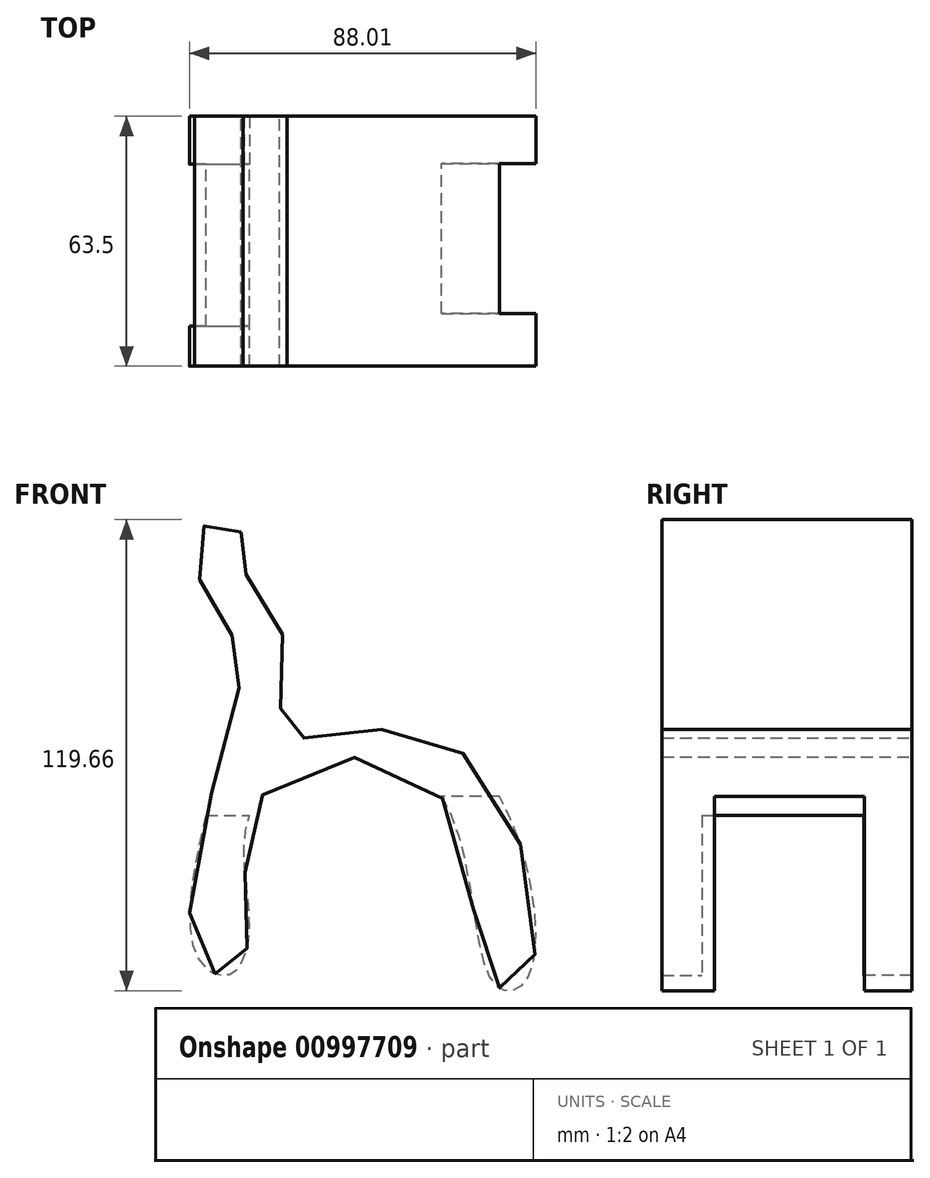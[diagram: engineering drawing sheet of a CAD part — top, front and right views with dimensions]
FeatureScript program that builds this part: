
annotation { "Feature Type Name" : "Feature", "Feature Type Description" : "" }
export const myFeature = defineFeature(function(context is Context, id is Id, definition is map)
    precondition{}
    {
        {
            var Q0;
            Q0=qCreatedBy(makeId("Front.planeOp"),FACE);
            var sketch = newSketch(context, id + "F0", { "sketchPlane" : qUnion([Q0])});
            skFitSpline(sketch, "E0", {"points": [v(-44.5, 57.5) * mm, v(-51.95, 60.33) * mm, v(-56.21, 49.33) * mm, v(-46.63, 30.89) * mm, v(-45.57, 15.64) * mm, v(-56.92, -47.15) * mm, v(-47.7, -54.95) * mm, v(-42.38, -42.18) * mm, v(-39.9, -10.26) * mm, v(3.02, -5.65) * mm, v(19.34, -56.72) * mm, v(28.2, -56.01) * mm, v(17.21, -3.87) * mm, v(-16.48, 6.77) * mm, v(-34.22, 6.77) * mm, v(-33.16, 28.4) * mm, v(-44.15, 48.98) * mm, v(-44.5, 57.5) * mm]});
            skSolve(sketch);
        }
        {
            var Q0;
            Q0=makeQuery(id+"F0.imprint","IMPRINT",FACE,{"disambiguationData":[TD([[makeQuery(id+"F0.imprint","IMPRINT",EDGE,{"derivedFrom":sQuery(id+"F0.wireOp",EDGE,"E0")}),1.0]])]});
            extrude(context, id + "F1", {"entities" : qUnion([Q0]), "depth" : 63.5 * mm, "offsetDistance" : 25.4 * mm});
        }
        {
            var Q0;
            Q0=qCreatedBy(makeId("Right.planeOp"),FACE);
            var sketch = newSketch(context, id + "F2", { "sketchPlane" : qUnion([Q0])});
            skLineSegment(sketch, "E1.bottom", {"start": v(-50.12, -9.67) * mm, "end": v(-12.03, -9.67) * mm});
            skLineSegment(sketch, "E1.top", {"start": v(-50.12, -61.45) * mm, "end": v(-12.03, -61.45) * mm});
            skLineSegment(sketch, "E1.left", {"start": v(-50.12, -9.67) * mm, "end": v(-50.12, -61.45) * mm});
            skLineSegment(sketch, "E1.right", {"start": v(-12.03, -9.67) * mm, "end": v(-12.03, -61.45) * mm});
            skSolve(sketch);
        }
        {
            var Q0;
            Q0=makeQuery(id+"F2.imprint","IMPRINT",FACE,{"disambiguationData":[TD([[makeQuery(id+"F2.imprint","IMPRINT",EDGE,{"derivedFrom":sQuery(id+"F2.wireOp",EDGE,"E1.bottom")}),-1.0]])]});
            extrude(context, id + "F3", {"entities" : qUnion([Q0]), "operationType" : NewBodyOperationType.REMOVE, "depth" : 45.97 * mm, "offsetDistance" : 25.4 * mm});
        }
        {
            var Q0;
            Q0=qCreatedBy(makeId("Right.planeOp"),FACE);
            var sketch = newSketch(context, id + "F4", { "sketchPlane" : qUnion([Q0])});
            skLineSegment(sketch, "E2.bottom", {"start": v(-12.16, -14.56) * mm, "end": v(-53.32, -14.56) * mm});
            skLineSegment(sketch, "E2.top", {"start": v(-12.16, -61.41) * mm, "end": v(-53.32, -61.41) * mm});
            skLineSegment(sketch, "E2.left", {"start": v(-12.16, -14.56) * mm, "end": v(-12.16, -61.41) * mm});
            skLineSegment(sketch, "E2.right", {"start": v(-53.32, -14.56) * mm, "end": v(-53.32, -61.41) * mm});
            skSolve(sketch);
        }
        {
            var Q0;
            Q0=makeQuery(id+"F4.imprint","IMPRINT",FACE,{"disambiguationData":[TD([[makeQuery(id+"F4.imprint","IMPRINT",EDGE,{"derivedFrom":sQuery(id+"F4.wireOp",EDGE,"E2.bottom")}),1.0]])]});
            extrude(context, id + "F5", {"entities" : qUnion([Q0]), "operationType" : NewBodyOperationType.REMOVE, "oppositeDirection" : true, "depth" : 87.12 * mm, "offsetDistance" : 25.4 * mm});
        }
    });
